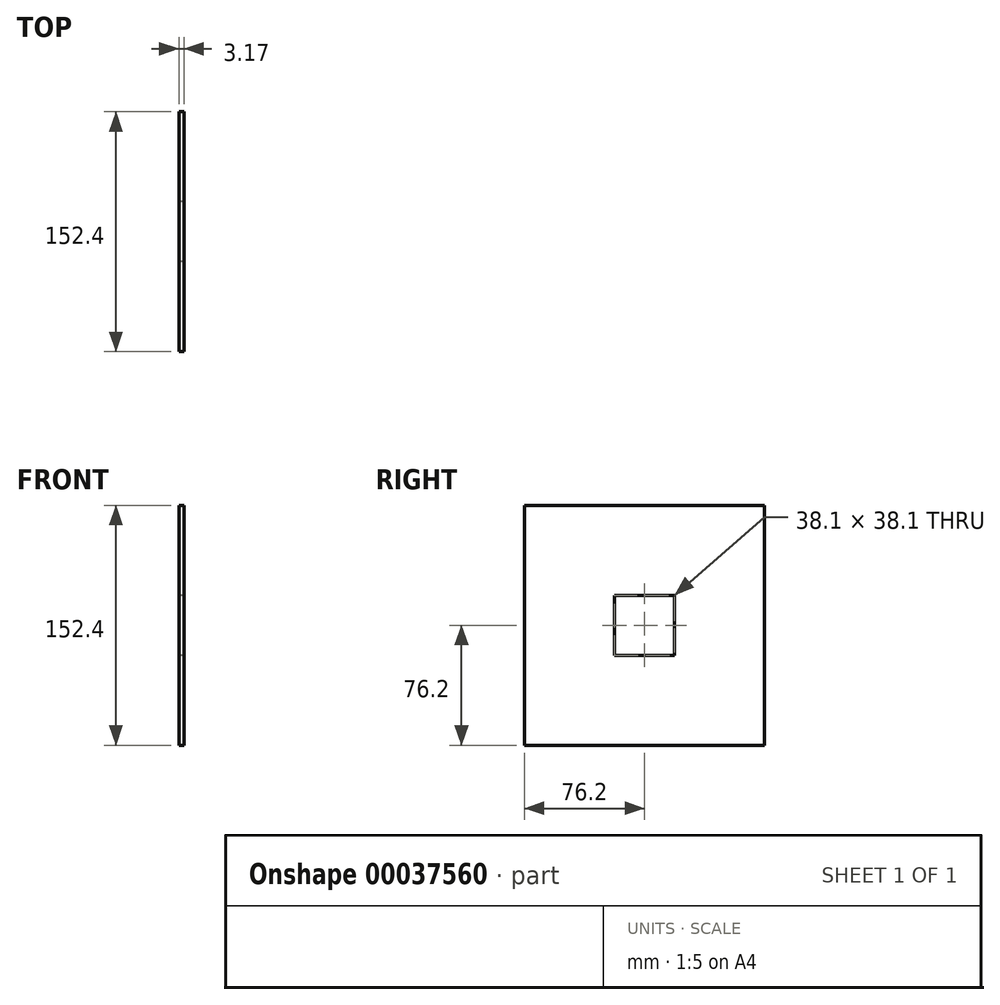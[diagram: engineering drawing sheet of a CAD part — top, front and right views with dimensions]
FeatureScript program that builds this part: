
annotation { "Feature Type Name" : "Feature", "Feature Type Description" : "" }
export const myFeature = defineFeature(function(context is Context, id is Id, definition is map)
    precondition{}
    {
        {
            var Q0;
            Q0=qCreatedBy(makeId("Right.planeOp"),FACE);
            var sketch = newSketch(context, id + "F0", { "sketchPlane" : qUnion([Q0])});
            skLineSegment(sketch, "E0.rect.bottom", {"start": v(76.2, -76.2) * mm, "end": v(-76.2, -76.2) * mm});
            skLineSegment(sketch, "E0.rect.top", {"start": v(76.2, 76.2) * mm, "end": v(-76.2, 76.2) * mm});
            skLineSegment(sketch, "E0.rect.left", {"start": v(76.2, -76.2) * mm, "end": v(76.2, 76.2) * mm});
            skLineSegment(sketch, "E0.rect.right", {"start": v(-76.2, -76.2) * mm, "end": v(-76.2, 76.2) * mm});
            skPoint(sketch, "E0.rect.middle", {"position": v(0, 0) * mm});
            skLineSegment(sketch, "E1.rect.bottom", {"start": v(19.05, -19.05) * mm, "end": v(-19.05, -19.05) * mm});
            skLineSegment(sketch, "E1.rect.top", {"start": v(19.05, 19.05) * mm, "end": v(-19.05, 19.05) * mm});
            skLineSegment(sketch, "E1.rect.left", {"start": v(19.05, -19.05) * mm, "end": v(19.05, 19.05) * mm});
            skLineSegment(sketch, "E1.rect.right", {"start": v(-19.05, -19.05) * mm, "end": v(-19.05, 19.05) * mm});
            skSolve(sketch);
        }
        {
            var Q0;
            Q0=makeQuery(id+"F0.imprint","IMPRINT",FACE,{"disambiguationData":[TD([[makeQuery(id+"F0.imprint","IMPRINT",EDGE,{"derivedFrom":sQuery(id+"F0.wireOp",EDGE,"E0.rect.bottom")}),-1.0]])]});
            extrude(context, id + "F1", {"entities" : qUnion([Q0]), "depth" : 3.17 * mm});
        }
    });
